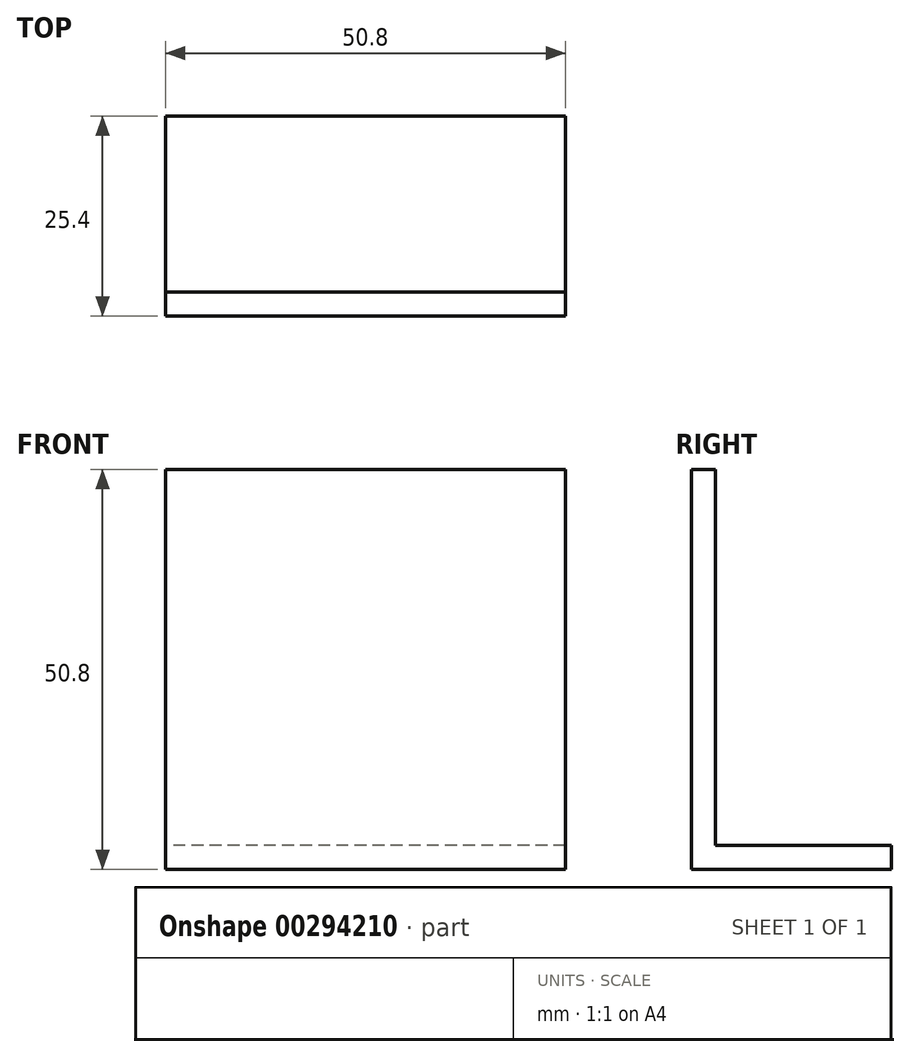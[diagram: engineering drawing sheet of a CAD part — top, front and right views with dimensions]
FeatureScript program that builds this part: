
annotation { "Feature Type Name" : "Feature", "Feature Type Description" : "" }
export const myFeature = defineFeature(function(context is Context, id is Id, definition is map)
    precondition{}
    {
        {
            var Q0;
            Q0=qCreatedBy(makeId("Right.planeOp"),FACE);
            var sketch = newSketch(context, id + "F0", { "sketchPlane" : qUnion([Q0])});
            skLineSegment(sketch, "E0", {"start": v(0, 0) * mm, "end": v(-25.4, 0) * mm});
            skLineSegment(sketch, "E1", {"start": v(-25.4, 0) * mm, "end": v(-25.4, 50.8) * mm});
            skLineSegment(sketch, "E2", {"start": v(-25.4, 50.8) * mm, "end": v(-22.35, 50.8) * mm});
            skLineSegment(sketch, "E3", {"start": v(-22.35, 50.8) * mm, "end": v(-22.35, 3.05) * mm});
            skLineSegment(sketch, "E4", {"start": v(-22.35, 3.05) * mm, "end": v(0, 3.05) * mm});
            skLineSegment(sketch, "E5", {"start": v(0, 3.05) * mm, "end": v(0, 0) * mm});
            skSolve(sketch);
        }
        {
            var Q0;
            Q0=makeQuery(id+"F0.imprint","IMPRINT",FACE,{"disambiguationData":[TD([[makeQuery(id+"F0.imprint","IMPRINT",EDGE,{"derivedFrom":sQuery(id+"F0.wireOp",EDGE,"E0")}),-1.0]])]});
            extrude(context, id + "F1", {"entities" : qUnion([Q0]), "depth" : 50.8 * mm});
        }
    });
